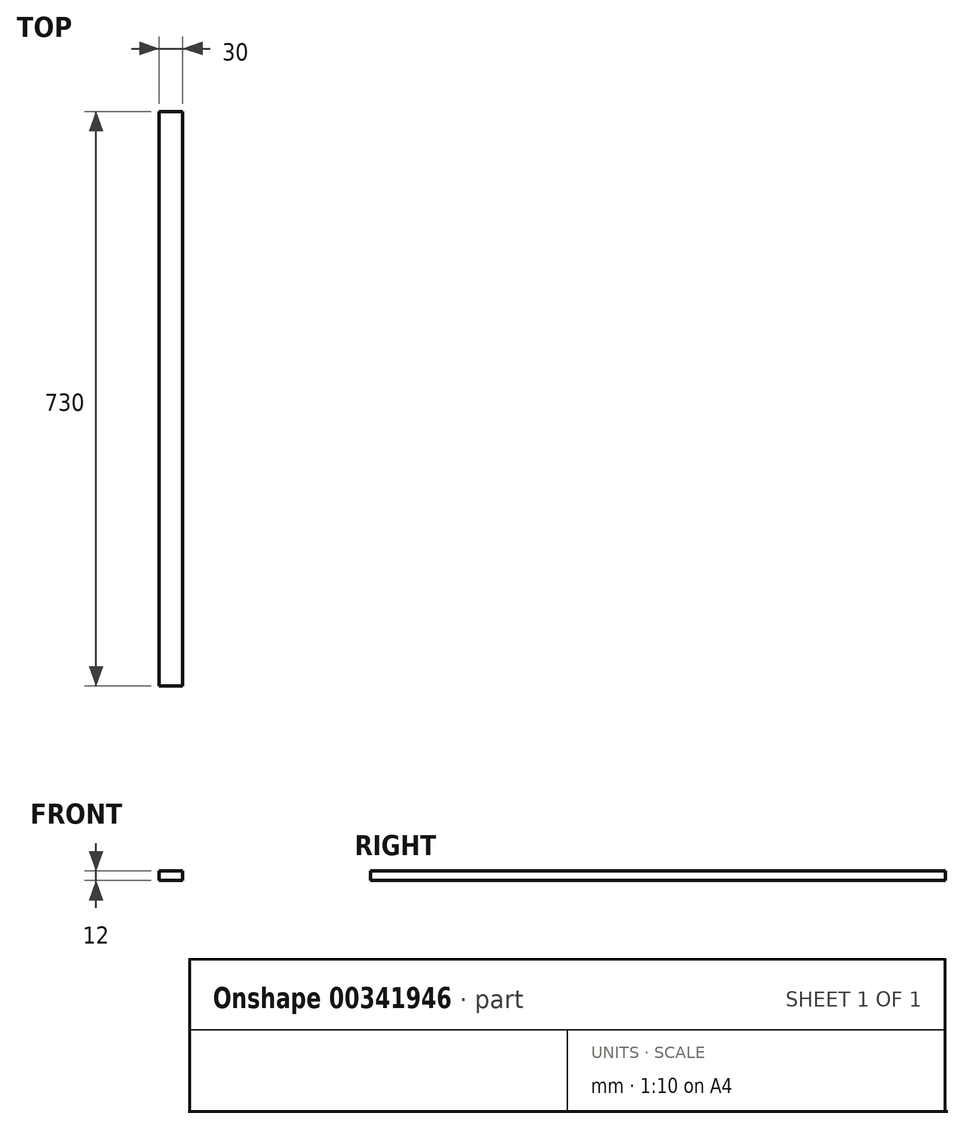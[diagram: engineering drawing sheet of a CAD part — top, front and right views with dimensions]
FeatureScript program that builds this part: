
annotation { "Feature Type Name" : "Feature", "Feature Type Description" : "" }
export const myFeature = defineFeature(function(context is Context, id is Id, definition is map)
    precondition{}
    {
        {
            var Q0;
            Q0=qCreatedBy(makeId("Front.planeOp"),FACE);
            var sketch = newSketch(context, id + "F0", { "sketchPlane" : qUnion([Q0])});
            skLineSegment(sketch, "E0.bottom", {"start": v(-15, 6) * mm, "end": v(15, 6) * mm});
            skLineSegment(sketch, "E0.top", {"start": v(-15, -6) * mm, "end": v(15, -6) * mm});
            skLineSegment(sketch, "E0.left", {"start": v(-15, 6) * mm, "end": v(-15, -6) * mm});
            skLineSegment(sketch, "E0.right", {"start": v(15, 6) * mm, "end": v(15, -6) * mm});
            skPoint(sketch, "E0.middle", {"position": v(0, 0) * mm});
            skSolve(sketch);
        }
        {
            var Q0;
            Q0=makeQuery(id+"F0.imprint","IMPRINT",FACE,{"disambiguationData":[TD([[makeQuery(id+"F0.imprint","IMPRINT",EDGE,{"derivedFrom":sQuery(id+"F0.wireOp",EDGE,"E0.bottom")}),-1.0]])]});
            extrude(context, id + "F1", {"entities" : qUnion([Q0]), "depth" : 365 * mm, "hasSecondDirection" : true, "secondDirectionOppositeDirection" : true, "secondDirectionDepth" : 365 * mm});
        }
    });
